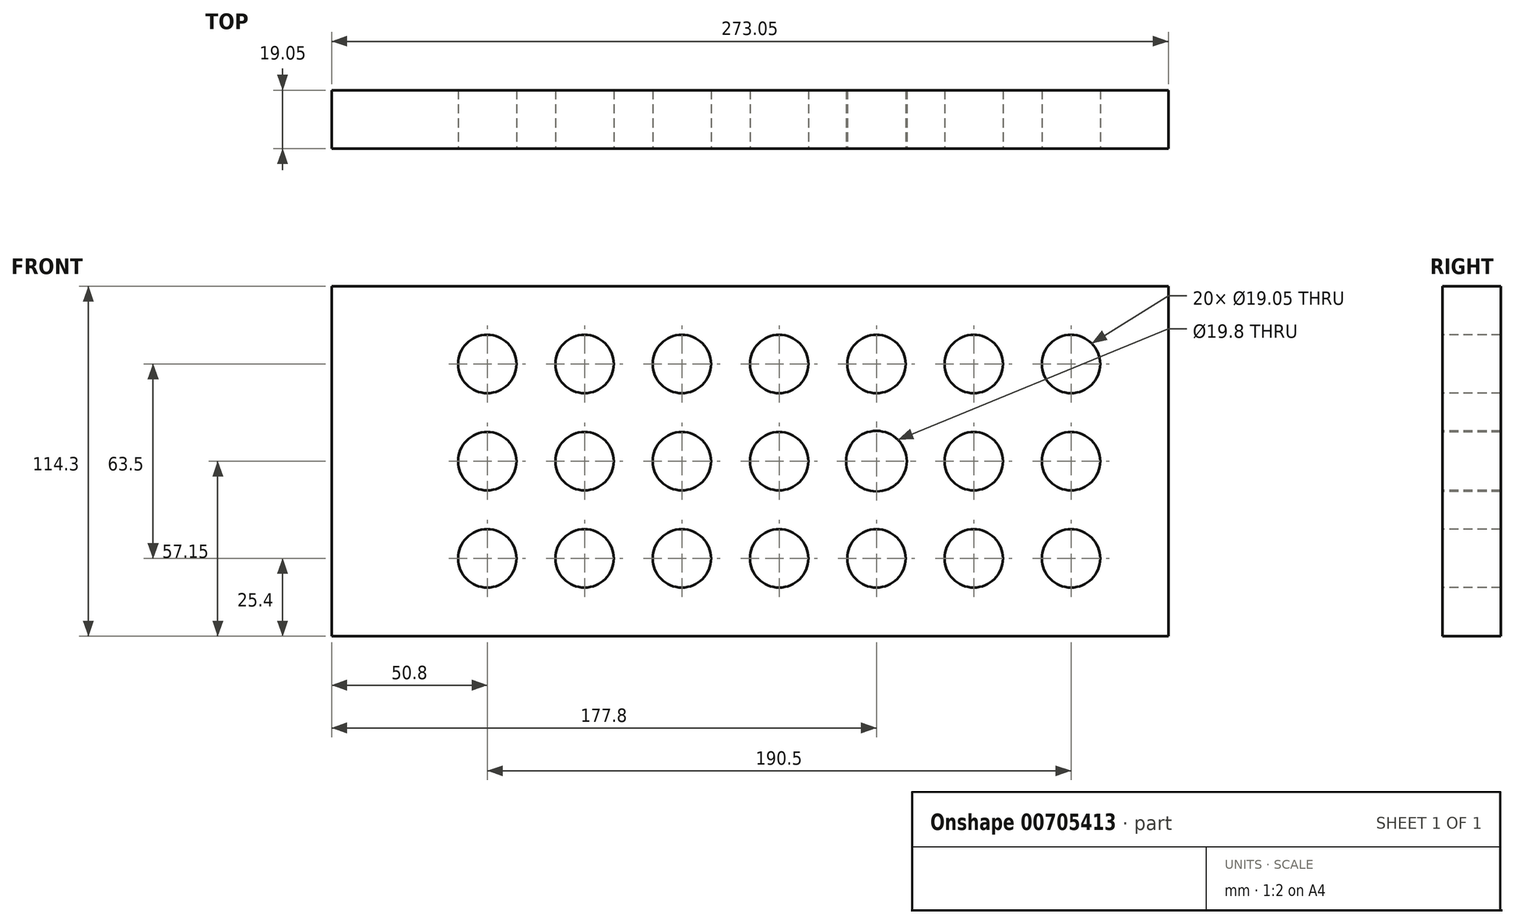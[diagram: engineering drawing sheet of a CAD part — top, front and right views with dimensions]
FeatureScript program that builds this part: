
annotation { "Feature Type Name" : "Feature", "Feature Type Description" : "" }
export const myFeature = defineFeature(function(context is Context, id is Id, definition is map)
    precondition{}
    {
        {
            var Q0;
            Q0=qCreatedBy(makeId("Front.planeOp"),FACE);
            var sketch = newSketch(context, id + "F0", { "sketchPlane" : qUnion([Q0])});
            skLineSegment(sketch, "E0.bottom", {"start": v(0, 0) * mm, "end": v(273.05, 0) * mm});
            skLineSegment(sketch, "E0.top", {"start": v(0, 114.3) * mm, "end": v(273.05, 114.3) * mm});
            skLineSegment(sketch, "E0.left", {"start": v(0, 0) * mm, "end": v(0, 114.3) * mm});
            skLineSegment(sketch, "E0.right", {"start": v(273.05, 0) * mm, "end": v(273.05, 114.3) * mm});
            skSolve(sketch);
        }
        {
            var Q0;
            Q0=qSketchRegion(id+"F0",true);
            extrude(context, id + "F1", {"entities" : qUnion([Q0]), "depth" : 19.05 * mm, "offsetDistance" : 25.4 * mm});
        }
        {
            var Q0;
            Q0=makeQuery(id+"F1.opExtrude","CAP_FACE",FACE,{"disambiguationData":[OSD([sQuery(id+"F0.wireOp",EDGE,"E0.bottom"),sQuery(id+"F0.wireOp",EDGE,"E0.top"),sQuery(id+"F0.wireOp",EDGE,"E0.left"),sQuery(id+"F0.wireOp",EDGE,"E0.right")])],"isStart":false});
            var sketch = newSketch(context, id + "F2", { "sketchPlane" : qUnion([Q0])});
            skCircle(sketch, "E1", {"center": v(50.8, 88.9) * mm, "radius": 9.53 * mm});
            skCircle(sketch, "E2", {"center": v(50.8, 57.15) * mm, "radius": 9.53 * mm});
            skCircle(sketch, "E3", {"center": v(82.55, 88.9) * mm, "radius": 9.53 * mm});
            skCircle(sketch, "E4", {"center": v(82.55, 57.15) * mm, "radius": 9.53 * mm});
            skCircle(sketch, "E5", {"center": v(114.3, 88.9) * mm, "radius": 9.53 * mm});
            skCircle(sketch, "E6", {"center": v(114.3, 57.15) * mm, "radius": 9.53 * mm});
            skCircle(sketch, "E7", {"center": v(50.8, 25.4) * mm, "radius": 9.53 * mm});
            skCircle(sketch, "E8", {"center": v(82.55, 25.4) * mm, "radius": 9.53 * mm});
            skCircle(sketch, "E9", {"center": v(114.3, 25.4) * mm, "radius": 9.53 * mm});
            skCircle(sketch, "E10", {"center": v(146.05, 88.9) * mm, "radius": 9.53 * mm});
            skCircle(sketch, "E11", {"center": v(146.05, 57.15) * mm, "radius": 9.53 * mm});
            skCircle(sketch, "E12", {"center": v(146.05, 25.4) * mm, "radius": 9.53 * mm});
            skCircle(sketch, "E13", {"center": v(177.8, 88.9) * mm, "radius": 9.53 * mm});
            skCircle(sketch, "E14", {"center": v(177.8, 57.15) * mm, "radius": 9.9 * mm});
            skCircle(sketch, "E15", {"center": v(177.8, 25.4) * mm, "radius": 9.53 * mm});
            skCircle(sketch, "E16", {"center": v(209.55, 88.9) * mm, "radius": 9.53 * mm});
            skCircle(sketch, "E17", {"center": v(209.55, 57.15) * mm, "radius": 9.53 * mm});
            skCircle(sketch, "E18", {"center": v(209.55, 25.4) * mm, "radius": 9.53 * mm});
            skCircle(sketch, "E19", {"center": v(241.3, 88.9) * mm, "radius": 9.53 * mm});
            skCircle(sketch, "E20", {"center": v(241.3, 57.15) * mm, "radius": 9.53 * mm});
            skCircle(sketch, "E21", {"center": v(241.3, 25.4) * mm, "radius": 9.53 * mm});
            skSolve(sketch);
        }
        {
            var Q0;
            Q0=qSketchRegion(id+"F2",true);
            extrude(context, id + "F3", {"entities" : qUnion([Q0]), "operationType" : NewBodyOperationType.REMOVE, "oppositeDirection" : true, "depth" : 25.4 * mm, "offsetDistance" : 25.4 * mm});
        }
    });
